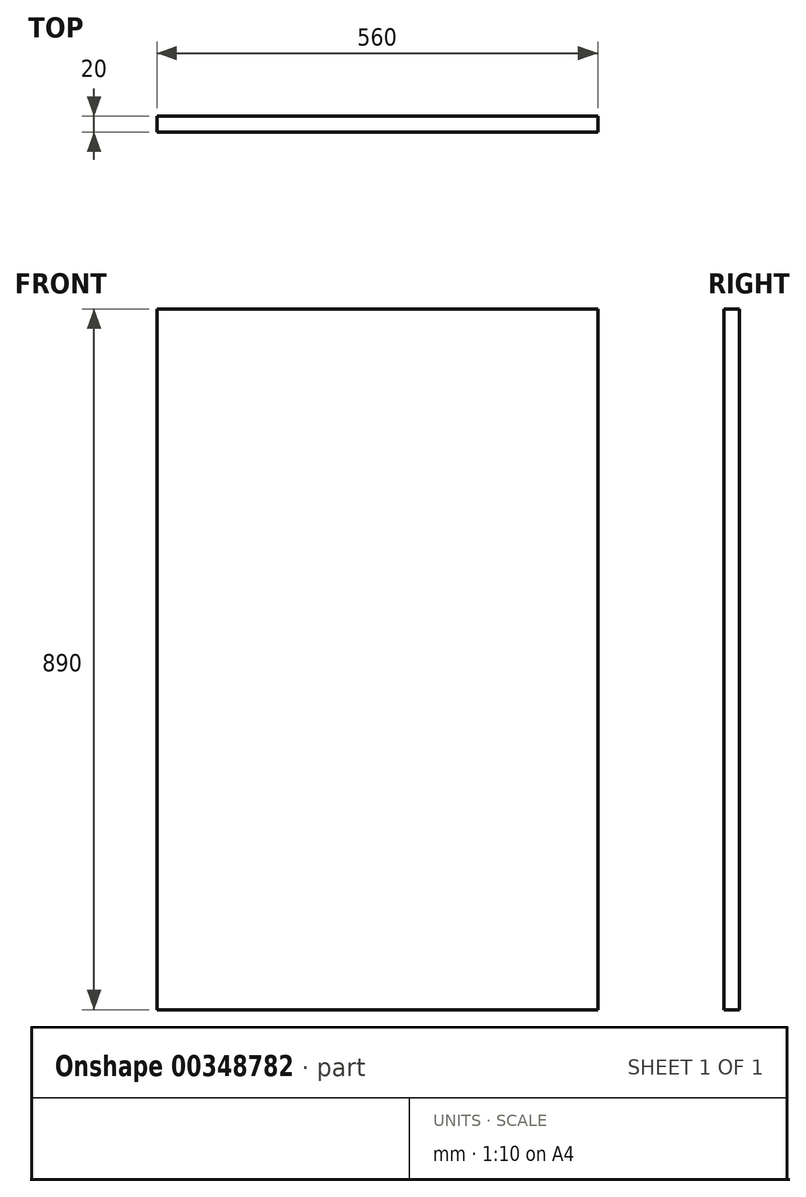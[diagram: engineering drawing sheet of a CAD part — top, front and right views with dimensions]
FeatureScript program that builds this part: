
annotation { "Feature Type Name" : "Feature", "Feature Type Description" : "" }
export const myFeature = defineFeature(function(context is Context, id is Id, definition is map)
    precondition{}
    {
        {
            var Q0;
            Q0=qCreatedBy(makeId("Front.planeOp"),FACE);
            var sketch = newSketch(context, id + "F0", { "sketchPlane" : qUnion([Q0])});
            skLineSegment(sketch, "E0.bottom", {"start": v(-560, -890) * mm, "end": v(0, -890) * mm});
            skLineSegment(sketch, "E0.top", {"start": v(-560, 0) * mm, "end": v(0, 0) * mm});
            skLineSegment(sketch, "E0.left", {"start": v(-560, -890) * mm, "end": v(-560, 0) * mm});
            skLineSegment(sketch, "E0.right", {"start": v(0, -890) * mm, "end": v(0, 0) * mm});
            skSolve(sketch);
        }
        {
            var Q0;
            Q0=qSketchRegion(id+"F0",true);
            extrude(context, id + "F1", {"entities" : qUnion([Q0]), "depth" : 20 * mm});
        }
    });
